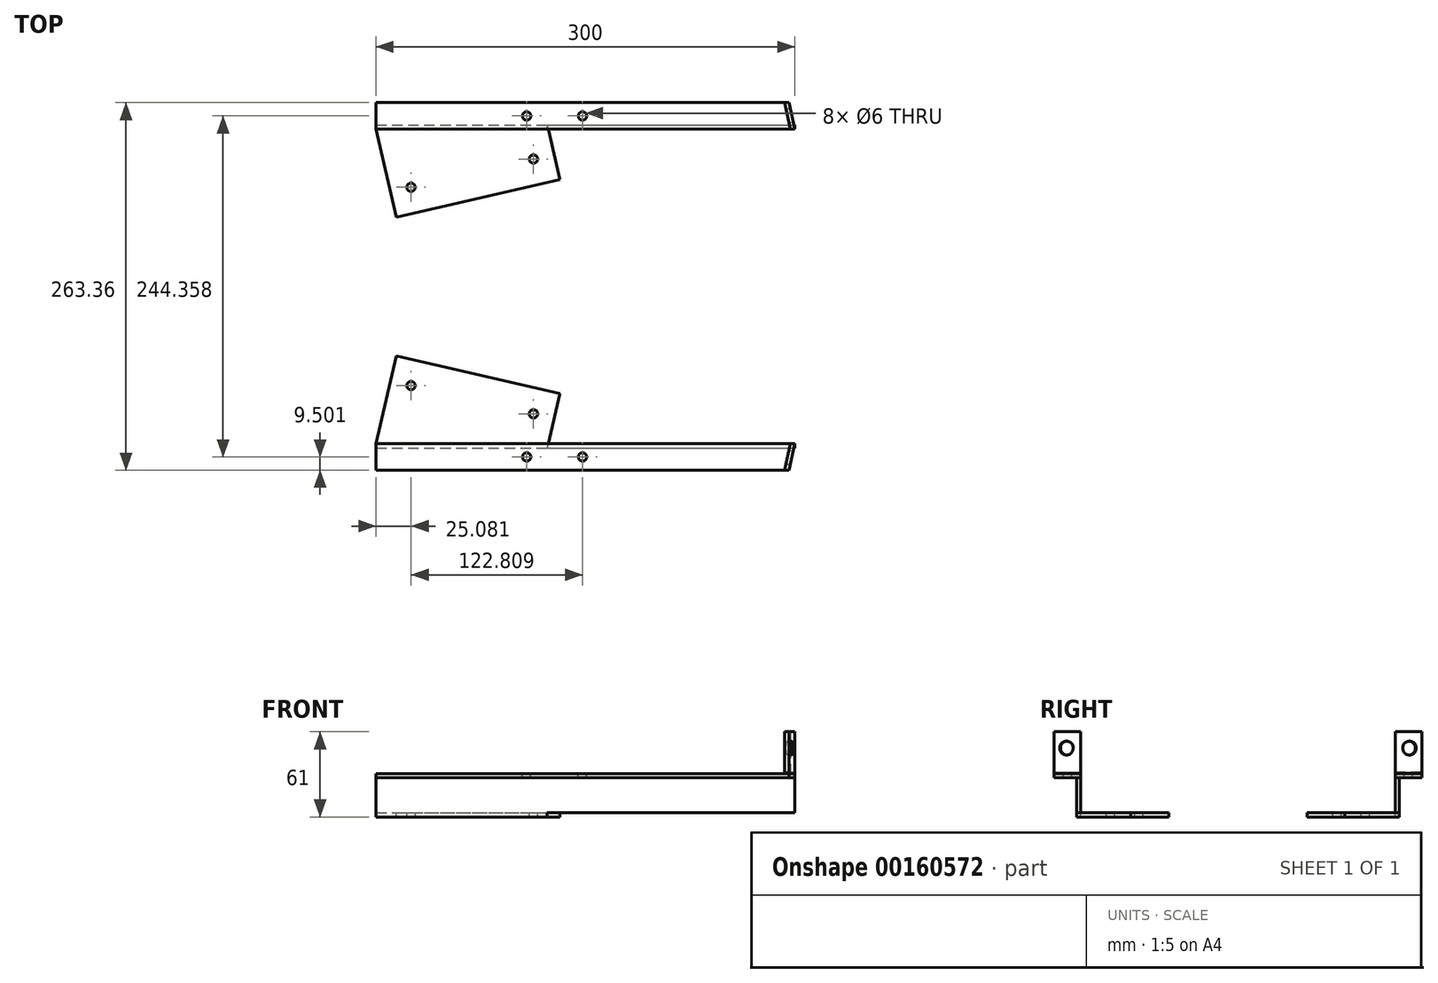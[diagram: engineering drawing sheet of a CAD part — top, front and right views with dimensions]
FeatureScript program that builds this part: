
annotation { "Feature Type Name" : "Feature", "Feature Type Description" : "" }
export const myFeature = defineFeature(function(context is Context, id is Id, definition is map)
    precondition{}
    {
        {
            var Q0;
            Q0=qCreatedBy(makeId("Top.planeOp"),FACE);
            var sketch = newSketch(context, id + "F0", { "sketchPlane" : qUnion([Q0])});
            skLineSegment(sketch, "E0.bottom", {"start": v(-118.62, 31.68) * mm, "end": v(181.38, 31.68) * mm});
            skLineSegment(sketch, "E0.top", {"start": v(-118.62, 12.68) * mm, "end": v(181.38, 12.68) * mm});
            skLineSegment(sketch, "E0.left", {"start": v(-118.62, 31.68) * mm, "end": v(-118.62, 12.68) * mm});
            skLineSegment(sketch, "E0.right", {"start": v(181.38, 31.68) * mm, "end": v(181.38, 12.68) * mm});
            skLineSegment(sketch, "E1", {"start": v(-118.62, 12.68) * mm, "end": v(-118.62, 15.68) * mm});
            skLineSegment(sketch, "E2", {"start": v(-118.62, 15.68) * mm, "end": v(181.38, 15.68) * mm});
            skSolve(sketch);
        }
        {
            var Q0;
            Q0=makeQuery(id+"F0.imprint","IMPRINT",FACE,{"disambiguationData":[TD([[makeQuery(id+"F0.imprint","IMPRINT",EDGE,{"derivedFrom":sQuery(id+"F0.wireOp",EDGE,"E0.bottom")}),-1.0]])]});
            var Q1;
            {var subQ0=sQuery(id+"F0.wireOp",EDGE,"E0.top");Q1=makeQuery(id+"F0.imprint","IMPRINT",FACE,{"disambiguationData":[TD([[makeQuery(id+"F0.imprint","IMPRINT",EDGE,{"derivedFrom":subQ0}),1.0]])]});}
            extrude(context, id + "F1", {"entities" : qUnion([Q0, Q1]), "depth" : 3 * mm});
        }
        {
            var Q0;
            Q0=makeQuery(id+"F1.opExtrude","CAP_FACE",FACE,{"disambiguationData":[OSD([sQuery(id+"F0.wireOp",EDGE,"E0.bottom"),sQuery(id+"F0.wireOp",EDGE,"E0.top"),sQuery(id+"F0.wireOp",EDGE,"E0.left"),sQuery(id+"F0.wireOp",EDGE,"E0.right")])],"isStart":false});
            var sketch = newSketch(context, id + "F2", { "sketchPlane" : qUnion([Q0])});
            skLineSegment(sketch, "E3", {"start": v(177.16, 31.68) * mm, "end": v(181.38, 12.68) * mm});
            skLineSegment(sketch, "E4", {"start": v(177.16, 31.68) * mm, "end": v(181.38, 31.68) * mm});
            skLineSegment(sketch, "E5", {"start": v(181.38, 31.68) * mm, "end": v(181.38, 12.68) * mm});
            skSolve(sketch);
        }
        {
            var Q0;
            Q0=makeQuery(id+"F2.imprint","IMPRINT",FACE,{"disambiguationData":[TD([[makeQuery(id+"F2.imprint","IMPRINT",EDGE,{"derivedFrom":sQuery(id+"F2.wireOp",EDGE,"E3")}),1.0]])]});
            extrude(context, id + "F3", {"entities" : qUnion([Q0]), "operationType" : NewBodyOperationType.REMOVE, "endBound" : BoundingType.THROUGH_ALL, "oppositeDirection" : true, "depth" : 25 * mm});
        }
        {
            var Q0;
            Q0=makeQuery(id+"F1.opExtrude","CAP_FACE",FACE,{"disambiguationData":[OSD([sQuery(id+"F0.wireOp",EDGE,"E0.bottom"),sQuery(id+"F0.wireOp",EDGE,"E0.top"),sQuery(id+"F0.wireOp",EDGE,"E0.left"),sQuery(id+"F0.wireOp",EDGE,"E0.right")])],"isStart":false});
            var sketch = newSketch(context, id + "F4", { "sketchPlane" : qUnion([Q0])});
            skLineSegment(sketch, "E6", {"start": v(174.1, 31.68) * mm, "end": v(178.3, 12.68) * mm});
            skLineSegment(sketch, "E7", {"start": v(179.27, 22.18) * mm, "end": v(29.27, 22.18) * mm, "construction": true});
            skLineSegment(sketch, "E8", {"start": v(29.27, 22.18) * mm, "end": v(-10.73, 22.18) * mm, "construction": true});
            skCircle(sketch, "E9", {"center": v(29.27, 22.18) * mm, "radius": 3 * mm});
            skCircle(sketch, "E10", {"center": v(-10.73, 22.18) * mm, "radius": 3 * mm});
            skSolve(sketch);
        }
        {
            var Q0;
            {var subQ0=sQuery(id+"F4.wireOp",EDGE,"E6");Q0=makeQuery(id+"F4.imprint","IMPRINT",FACE,{"disambiguationData":[TD([[makeQuery(id+"F4.imprint","IMPRINT",EDGE,{"derivedFrom":subQ0}),1.0]])]});}
            extrude(context, id + "F5", {"entities" : qUnion([Q0]), "depth" : 30 * mm});
        }
        {
            var Q0;
            Q0=makeQuery(id+"F5.opExtrude","CAP_EDGE",EDGE,{"disambiguationData":[OSD([sQuery(id+"F4.wireOp",EDGE,"E6")])],"isStart":true});
            chamfer(context, id + "F6", {"entities" : qUnion([Q0]), "chamferType" : ChamferType.OFFSET_ANGLE, "width" : 5 * mm, "oppositeDirection" : true, "angle" : 10 * degree, "tangentPropagation" : true});
        }
        {
            var Q0;
            Q0=makeQuery(id+"F5.opExtrude","SWEPT_FACE",FACE,{"disambiguationData":[OSD([sQuery(id+"F2.wireOp",EDGE,"E3")])]});
            var sketch = newSketch(context, id + "F7", { "sketchPlane" : qUnion([Q0])});
            skLineSegment(sketch, "E11", {"start": v(-17.15, 3.35) * mm, "end": v(-17.15, 21.35) * mm});
            skCircle(sketch, "E12", {"center": v(-16.42, 21.35) * mm, "radius": 5 * mm});
            skSolve(sketch);
        }
        {
            var Q0;
            Q0=makeQuery(id+"F7.imprint","IMPRINT",FACE,{"disambiguationData":[TD([[makeQuery(id+"F7.imprint","IMPRINT",EDGE,{"derivedFrom":sQuery(id+"F7.wireOp",EDGE,"E12")}),1.0]])]});
            extrude(context, id + "F8", {"entities" : qUnion([Q0]), "operationType" : NewBodyOperationType.REMOVE, "endBound" : BoundingType.THROUGH_ALL, "oppositeDirection" : true, "depth" : 25 * mm});
        }
        {
            var Q0;
            Q0=qCreatedBy(makeId("Front.planeOp"),FACE);
            cPlane(context, id + "F9", {"entities" : qUnion([Q0]), "cplaneType" : CPlaneType.OFFSET, "offset" : 100 * mm, "width" : 150 * mm, "height" : 150 * mm});
        }
        {
            var Q0;
            {var subQ0=sQuery(id+"F0.wireOp",EDGE,"E0.top");Q0=makeQuery(id+"F0.imprint","IMPRINT",FACE,{"disambiguationData":[TD([[makeQuery(id+"F0.imprint","IMPRINT",EDGE,{"derivedFrom":subQ0}),1.0]])]});}
            extrude(context, id + "F10", {"entities" : qUnion([Q0]), "operationType" : NewBodyOperationType.ADD, "oppositeDirection" : true, "depth" : 25 * mm});
        }
        {
            var Q0;
            Q0=makeQuery(id+"F10.opExtrude","CAP_FACE",FACE,{"disambiguationData":[OSD([sQuery(id+"F0.wireOp",EDGE,"E0.top"),sQuery(id+"F0.wireOp",EDGE,"E0.right"),sQuery(id+"F0.wireOp",EDGE,"E1"),sQuery(id+"F0.wireOp",EDGE,"E2")])],"isStart":false});
            var sketch = newSketch(context, id + "F11", { "sketchPlane" : qUnion([Q0])});
            skLineSegment(sketch, "E13", {"start": v(-118.62, -12.68) * mm, "end": v(-104.08, 50.33) * mm});
            skLineSegment(sketch, "E14", {"start": v(-104.08, 50.33) * mm, "end": v(13, 23.3) * mm});
            skLineSegment(sketch, "E15", {"start": v(13, 23.3) * mm, "end": v(4.7, -12.68) * mm});
            skLineSegment(sketch, "E16", {"start": v(8.85, 5.29) * mm, "end": v(-108.23, 32.32) * mm, "construction": true});
            skCircle(sketch, "E17", {"center": v(-93.54, 28.93) * mm, "radius": 3 * mm});
            skCircle(sketch, "E18", {"center": v(-5.85, 8.68) * mm, "radius": 3 * mm});
            skLineSegment(sketch, "E19", {"start": v(-93.54, 28.93) * mm, "end": v(-108.23, 32.32) * mm, "construction": true});
            skLineSegment(sketch, "E20", {"start": v(-5.85, 8.68) * mm, "end": v(8.85, 5.29) * mm, "construction": true});
            skLineSegment(sketch, "E21", {"start": v(-118.62, -12.68) * mm, "end": v(-119.32, -15.68) * mm});
            skLineSegment(sketch, "E22", {"start": v(4.7, -12.68) * mm, "end": v(4, -15.68) * mm});
            skLineSegment(sketch, "E23", {"start": v(-118.62, -12.68) * mm, "end": v(-118.62, -12.68) * mm});
            skSolve(sketch);
        }
        {
            var Q0;
            {var subQ1=sQuery(id+"F11.wireOp",EDGE,"E13");Q0=makeQuery(id+"F11.imprint","IMPRINT",FACE,{"disambiguationData":[TD([[makeQuery(id+"F11.imprint","IMPRINT",EDGE,{"derivedFrom":subQ1}),-1.0]])]});}
            var Q1;
            {var subQ0=sQuery(id+"F11.wireOp",EDGE,"E22");Q1=makeQuery(id+"F11.imprint","IMPRINT",FACE,{"disambiguationData":[TD([[makeQuery(id+"F11.imprint","IMPRINT",EDGE,{"derivedFrom":subQ0}),-1.0]])]});}
            extrude(context, id + "F12", {"entities" : qUnion([Q0, Q1]), "operationType" : NewBodyOperationType.ADD, "depth" : 3 * mm});
        }
        {
            var Q0;
            Q0=makeQuery(id+"F4.imprint","IMPRINT",FACE,{"disambiguationData":[TD([[makeQuery(id+"F4.imprint","IMPRINT",EDGE,{"derivedFrom":sQuery(id+"F4.wireOp",EDGE,"E9")}),1.0]])]});
            var Q1;
            Q1=makeQuery(id+"F4.imprint","IMPRINT",FACE,{"disambiguationData":[TD([[makeQuery(id+"F4.imprint","IMPRINT",EDGE,{"derivedFrom":sQuery(id+"F4.wireOp",EDGE,"E10")}),1.0]])]});
            extrude(context, id + "F13", {"entities" : qUnion([Q0, Q1]), "operationType" : NewBodyOperationType.REMOVE, "endBound" : BoundingType.THROUGH_ALL, "oppositeDirection" : true, "depth" : 25 * mm});
        }
        {
            var Q0;
            Q0=makeQuery(id+"F1.opExtrude","SWEPT_BODY",BODY,{"disambiguationData":[OSD([sQuery(id+"F0.wireOp",EDGE,"E0.bottom"),sQuery(id+"F0.wireOp",EDGE,"E0.top"),sQuery(id+"F0.wireOp",EDGE,"E0.left"),sQuery(id+"F0.wireOp",EDGE,"E0.right")])]});
            var Q1;
            Q1=makeQuery(id+"F5.opExtrude","SWEPT_BODY",BODY,{"disambiguationData":[OSD([sQuery(id+"F0.wireOp",EDGE,"E0.bottom"),sQuery(id+"F0.wireOp",EDGE,"E0.top"),sQuery(id+"F2.wireOp",EDGE,"E3"),sQuery(id+"F4.wireOp",EDGE,"E6")])]});
            var Q2;
            Q2=qCreatedBy(id+"F9.planeOp",FACE);
            mirror(context, id + "F14", {"entities" : qUnion([Q0, Q1]), "mirrorPlane" : qUnion([Q2])});
        }
    });
